# Revit family: ORZH-1-6 Doors-ALL
name_source: partatom
category: Mechanical Equipment
units: mm (PartAtom-declared; Revit-internal decimal feet)

## family parameters
Always vertical = Yes
Cut with Voids When Loaded = No
OmniClass Number = 23.40.40.11.17
OmniClass Title = Refrigerated Cases
Part Type = Normal
Room Calculation Point = No
Round Connector Dimension = Use Radius
Shared = No
Work Plane-Based = Yes

## types (6) — shared parameters
101 Amps = 0 A
27" Shelf = Yes
30" x 64" 1 Door = Yes
Certifications = NSF 7, UL471, CSA
DATE = 12/21/2015
DISCHARGE AIR TEMP = 380 °F
DISCHARGE AIR VELOCITY = 34 °F
Default Elevation = 48"
Defrost Num Day = 4
Defrost Termination = 47 °F
Defrost Type = TIMED-OFF DEFROST
Defrosts Per Day_2 = 1
Description = HIGH REACH-IN GLASS DOOR MERCHANIDER
Discharge Air Velocity (FPM) = 350 (FPM)
EQUIPMENT DESCRIPTION = HIGH REACH-IN GLASS DOOR MERCHANIDER
EQUIPMENT MARK = ORZH
Electric Defrost Fail-Safe = 46 (Min)
Electric Defrost Run-Off Time (Min) = 0 (Min)
Electric Defrost Termination Temp (°F) = 50° F
Evap Temp = 28
GLASS = Glass
Heated/Low E = Heated
Height = 85 1/4"
Hot Gas Defrost Fail-Safe = 24 (Min)
Hot Gas Defrost Run-Off Time (Min) = 13-15 (Min)
Hot Gas Defrost Termination = 73° F
Hot Gas Defrost Termination Temp (°F) = 73 °F
Item Description = HIGH REACH-IN GLASS DOOR MERCHANIDER
Legend Number = ORZH
Load Mbh = 0.675
METAL = <By Category>
Manufacturer = HILL PHOENIX
Model = ORZH
PAINTED METAL UPPER SHELF = PAINTED SHELVES
Refrig Charge Lbs = 0
Size of Door = 30"
Superheat Set Point @ Bulb (°F) = 3-5° F
URL = http://www.hillphoenix.com
Width = 42"
set 3 biswing doors = No
zero-valued in all types: Lights Per Row

## per-type parameters (varying)
- 2-Door-30"-Frozen-Heated: 101-LE DOOR FRAME AMPS=1 A; 101-LE DOOR FRAME WATTS=151 W; Application Discipline=Frozen; BTUH Conventional=1044; BTUH Parallel=1014; CENTER LINE & DRAIN=30"; Combined Heated Rails Amps=2 A; Combined Heated Rails Watts=219 W; Combined Low E Rails Amps=2 A; Combined Low E Rails Watts=192 W; DOOR CONFIGURATION=MASTER DOOR : 30" X 68 3/8" 2 DOOR A SWING (LEFT OPENING); DRAIN HEATER AMPS=1 A; DRAIN HEATER WATTS=152 W; Defrost (Phase 1) 208 V Amps=8 A; Defrost (Phase 1) 208 V Watts=1552 W; Defrost (Phase 1) 240 V Amps=9 A; Defrost (Phase 1) 240 V Watts=2068 W; Defrost (Phase 3) 208 V Amps=7 A; Defrost (Phase 3) 208 V Watts=1552 W; Defrost (Phase 3) 240 V Amps=8 A; Defrost (Phase 3) 240 V Watts=2068 W; Discharge Air (°F)=-1; Evaporator (°F)=-7; GE Immersion Amps=0 A; GE Immersion Watts=32 W; HEATED DOORS AMPS=1 A; HEATED DOORS WATTS=76 W; Heated Option (IG and Rails) Amps=1 A; Heated Option (IG and Rails) Watts=67 W; High Efficiency Amps=1 A; High Efficiency Watts=50 W; Individual 101-LE Frame Amps=1 A; Individual 101-LE Frame Watts=151 W; Individual Heated Doors Amps=1 A; Individual Heated Doors Watts=67 W; Individual Low E Doors Amps=0 A; Individual Low E Doors Watts=41 W; LOW E DOORS AMPS=0 A; LOW E DOORS WATTS=45 W; LOW E RAILS AMPS=0 A; LOW E RAILS WATTS=40 W; Length=60"; Length of Cases=60"; NUMBER FOR GUIDLINES AND CONTROL ORGANIZATION=1; NUMBER OF DOORS=2; Number of Fans=2; Optimax Pro Amps=0 A; Optimax Pro Watts=43 W; Tank/Drain Heater Amps=1 A; Tank/Drain Heater Watts=152 W; Type of Door Swing=B-Swing; right side single door=No; set 1 biswing doors=Yes; set 2 biswing doors=No
- 3-Door-30"-Frozen-Heated: 101-LE DOOR FRAME AMPS=2 A; 101-LE DOOR FRAME WATTS=211 W; Application Discipline=Frozen; BTUH Conventional=988; BTUH Parallel=960; CENTER LINE & DRAIN=45"; Combined Heated Rails Amps=3 A; Combined Heated Rails Watts=312 W; Combined Low E Rails Amps=2 A; Combined Low E Rails Watts=272 W; DOOR CONFIGURATION=MASTER DOOR : 30" X 68 3/8" 3 DOOR A SWING (LEFT OPENING); DRAIN HEATER AMPS=2 A; DRAIN HEATER WATTS=171 W; Defrost (Phase 1) 208 V Amps=11 A; Defrost (Phase 1) 208 V Watts=2274 W; Defrost (Phase 1) 240 V Amps=13 A; Defrost (Phase 1) 240 V Watts=3018 W; Defrost (Phase 3) 208 V Amps=10 A; Defrost (Phase 3) 208 V Watts=2274 W; Defrost (Phase 3) 240 V Amps=11 A; Defrost (Phase 3) 240 V Watts=3018 W; Discharge Air (°F)=-1; Evaporator (°F)=-7; GE Immersion Amps=0 A; GE Immersion Watts=48 W; HEATED DOORS AMPS=1 A; HEATED DOORS WATTS=114 W; Heated Option (IG and Rails) Amps=1 A; Heated Option (IG and Rails) Watts=101 W; High Efficiency Amps=1 A; High Efficiency Watts=75 W; Individual 101-LE Frame Amps=2 A; Individual 101-LE Frame Watts=211 W; Individual Heated Doors Amps=1 A; Individual Heated Doors Watts=1 W; Individual Low E Doors Amps=1 A; Individual Low E Doors Watts=61 W; LOW E DOORS AMPS=1 A; LOW E DOORS WATTS=68 W; LOW E RAILS AMPS=1 A; LOW E RAILS WATTS=61 W; Length=90"; Length of Cases=90"; NUMBER FOR GUIDLINES AND CONTROL ORGANIZATION=1; NUMBER OF DOORS=3; Number of Fans=3; Optimax Pro Amps=1 A; Optimax Pro Watts=65 W; Tank/Drain Heater Amps=2 A; Tank/Drain Heater Watts=171 W; Type of Door Swing=A-Swing; right side single door=Yes; set 1 biswing doors=No; set 2 biswing doors=No
- 4-Door-30"-Frozen-Heated: 101-LE DOOR FRAME AMPS=2 A; 101-LE DOOR FRAME WATTS=275 W; Application Discipline=Ice Cream; BTUH Conventional=1091; BTUH Parallel=1060; CENTER LINE & DRAIN=60"; Combined Heated Rails Amps=4 A; Combined Heated Rails Watts=410 W; Combined Low E Rails Amps=3 A; Combined Low E Rails Watts=356 W; DOOR CONFIGURATION=MASTER DOOR : 30" X 68 3/8" 4 DOOR A SWING (LEFT OPENING); DRAIN HEATER AMPS=2 A; DRAIN HEATER WATTS=226 W; Defrost (Phase 1) 208 V Amps=14 A; Defrost (Phase 1) 208 V Watts=2984 W; Defrost (Phase 1) 240 V Amps=17 A; Defrost (Phase 1) 240 V Watts=3992 W; Defrost (Phase 3) 208 V Amps=12 A; Defrost (Phase 3) 208 V Watts=2984 W; Defrost (Phase 3) 240 V Amps=14 A; Defrost (Phase 3) 240 V Watts=3392 W; Discharge Air (°F)=-8; Evaporator (°F)=-15; GE Immersion Amps=1 A; GE Immersion Watts=64 W; HEATED DOORS AMPS=1 A; HEATED DOORS WATTS=152 W; Heated Option (IG and Rails) Amps=1 A; Heated Option (IG and Rails) Watts=135 W; High Efficiency Amps=1 A; High Efficiency Watts=100 W; Individual 101-LE Frame Amps=2 A; Individual 101-LE Frame Watts=275 W; Individual Heated Doors Amps=2 A; Individual Heated Doors Watts=2 W; Individual Low E Doors Amps=1 A; Individual Low E Doors Watts=82 W; LOW E DOORS AMPS=1 A; LOW E DOORS WATTS=91 W; LOW E RAILS AMPS=1 A; LOW E RAILS WATTS=81 W; Length=120"; Length of Cases=120"; NUMBER FOR GUIDLINES AND CONTROL ORGANIZATION=1; NUMBER OF DOORS=4; Number of Fans=4; Optimax Pro Amps=1 A; Optimax Pro Watts=87 W; Tank/Drain Heater Amps=2 A; Tank/Drain Heater Watts=226 W; Type of Door Swing=B-Swing; right side single door=No; set 1 biswing doors=No; set 2 biswing doors=Yes
- 5-Door-30"-Frozen-Heated: 101-LE DOOR FRAME AMPS=3 A; 101-LE DOOR FRAME WATTS=334 W; Application Discipline=Ice Cream; BTUH Conventional=1027; BTUH Parallel=998; CENTER LINE & DRAIN=75"; Combined Heated Rails Amps=5 A; Combined Heated Rails Watts=502 W; Combined Low E Rails Amps=4 A; Combined Low E Rails Watts=436 W; DOOR CONFIGURATION=MASTER DOOR : 30" X 68 3/8" 5 DOOR A SWING (LEFT OPENING); DRAIN HEATER AMPS=2 A; DRAIN HEATER WATTS=275 W; Defrost (Phase 1) 208 V Amps=18 A; Defrost (Phase 1) 208 V Watts=3640 W; Defrost (Phase 1) 240 V Amps=20 A; Defrost (Phase 1) 240 V Watts=4840 W; Defrost (Phase 3) 208 V Amps=15 A; Defrost (Phase 3) 208 V Watts=3640 W; Defrost (Phase 3) 240 V Amps=17 A; Defrost (Phase 3) 240 V Watts=4840 W; Discharge Air (°F)=-8; Evaporator (°F)=-15; GE Immersion Amps=1 A; GE Immersion Watts=80 W; HEATED DOORS AMPS=2 A; HEATED DOORS WATTS=191 W; Heated Option (IG and Rails) Amps=1 A; Heated Option (IG and Rails) Watts=169 W; High Efficiency Amps=2 A; High Efficiency Watts=125 W; Individual 101-LE Frame Amps=3 A; Individual 101-LE Frame Watts=334 W; Individual Heated Doors Amps=2 A; Individual Heated Doors Watts=195 W; Individual Low E Doors Amps=1 A; Individual Low E Doors Watts=102 W; LOW E DOORS AMPS=1 A; LOW E DOORS WATTS=114 W; LOW E RAILS AMPS=1 A; LOW E RAILS WATTS=101 W; Length=150"; Length of Cases=150"; NUMBER FOR GUIDLINES AND CONTROL ORGANIZATION=1; NUMBER OF DOORS=5; Number of Fans=5; Optimax Pro Amps=1 A; Optimax Pro Watts=109 W; Tank/Drain Heater Amps=2 A; Tank/Drain Heater Watts=275 W; Type of Door Swing=B-Swing; right side single door=No; set 1 biswing doors=Yes; set 2 biswing doors=No
- 6-Door-30"-Frozen-Heated: 101-LE DOOR FRAME AMPS=3 A; 101-LE DOOR FRAME WATTS=394 W; Application Discipline=Frozen; BTUH Conventional=1044; BTUH Parallel=1014; CENTER LINE & DRAIN=90"; Combined Heated Rails Amps=6 A; Combined Heated Rails Watts=596 W; Combined Low E Rails Amps=4 A; Combined Low E Rails Watts=516 W; DOOR CONFIGURATION=MASTER DOOR : 30" X 68 3/8" 6 DOOR A SWING (LEFT OPENING); DRAIN HEATER AMPS=3 A; DRAIN HEATER WATTS=320 W; Defrost (Phase 1) 208 V Amps=20 A; Defrost (Phase 1) 208 V Watts=4224 W; Defrost (Phase 1) 240 V Amps=23 A; Defrost (Phase 1) 240 V Watts=5624 W; Defrost (Phase 3) 208 V Amps=18 A; Defrost (Phase 3) 208 V Watts=4224 W; Defrost (Phase 3) 240 V Amps=20 A; Defrost (Phase 3) 240 V Watts=5624 W; Discharge Air (°F)=-1° F; Evaporator (°F)=-7° F; GE Immersion Amps=1 A; GE Immersion Watts=96 W; HEATED DOORS AMPS=2 A; HEATED DOORS WATTS=229 W; Heated Option (IG and Rails) Amps=2 A; Heated Option (IG and Rails) Watts=202 W; High Efficiency Amps=2 A; High Efficiency Watts=150 W; Individual 101-LE Frame Amps=3 A; Individual 101-LE Frame Watts=394 W; Individual Heated Doors Amps=2 A; Individual Heated Doors Watts=234 W; Individual Low E Doors Amps=1 A; Individual Low E Doors Watts=122 W; LOW E DOORS AMPS=1 A; LOW E DOORS WATTS=136 W; LOW E RAILS AMPS=1 A; LOW E RAILS WATTS=121 W; Length=180"; Length of Cases=180"; NUMBER FOR GUIDLINES AND CONTROL ORGANIZATION=0; NUMBER OF DOORS=6; Number of Fans=6; Optimax Pro Amps=1 A; Optimax Pro Watts=132 W; Tank/Drain Heater Amps=3 A; Tank/Drain Heater Watts=320 W; Type of Door Swing=B-Swing; right side single door=Yes; set 1 biswing doors=Yes; set 2 biswing doors=No
- 1-Door-Frozen Heated: 101-LE DOOR FRAME AMPS=1 A; 101-LE DOOR FRAME WATTS=91 W; Application Discipline=Frozen; BTUH Conventional=1044; BTUH Parallel=1014; CENTER LINE & DRAIN=15"; Combined Heated Rails Amps=2 A; Combined Heated Rails Watts=219 W; Combined Low E Rails Amps=2 A; Combined Low E Rails Watts=192 W; DOOR CONFIGURATION=MASTER DOOR : 30" X 68 3/8" 1 DOOR A SWING (LEFT OPENING); DRAIN HEATER AMPS=1 A; DRAIN HEATER WATTS=113 W; Defrost (Phase 1) 208 V Amps=3 A; Defrost (Phase 1) 208 V Watts=680 W; Defrost (Phase 1) 240 V Amps=4 A; Defrost (Phase 1) 240 V Watts=906 W; Defrost (Phase 3) 208 V Amps=3 A; Defrost (Phase 3) 208 V Watts=680 W; Defrost (Phase 3) 240 V Amps=3 A; Defrost (Phase 3) 240 V Watts=906 W; Discharge Air (°F)=-1° F; Evaporator (°F)=-7° F; GE Immersion Amps=0 A; GE Immersion Watts=16 W; HEATED DOORS AMPS=0 A; HEATED DOORS WATTS=38 W; Heated Option (IG and Rails) Amps=0 A; Heated Option (IG and Rails) Watts=34 W; High Efficiency Amps=0 A; High Efficiency Watts=25 W; Individual 101-LE Frame Amps=1 A; Individual 101-LE Frame Watts=151 W; Individual Heated Doors Amps=1 A; Individual Heated Doors Watts=67 W; Individual Low E Doors Amps=0 A; Individual Low E Doors Watts=41 W; LOW E DOORS AMPS=0 A; LOW E DOORS WATTS=23 W; LOW E RAILS AMPS=0 A; LOW E RAILS WATTS=20 W; Length=30"; Length of Cases=31"; NUMBER FOR GUIDLINES AND CONTROL ORGANIZATION=0; NUMBER OF DOORS=1; Number of Fans=1; Optimax Pro Amps=0 A; Optimax Pro Watts=21 W; Tank/Drain Heater Amps=1 A; Tank/Drain Heater Watts=152 W; Type of Door Swing=B-Swing; right side single door=No; set 1 biswing doors=Yes; set 2 biswing doors=No

## geometry (parser evidence)
native form markers: Blend x10, Sweep x28
no freeform markers — native parametric forms only
